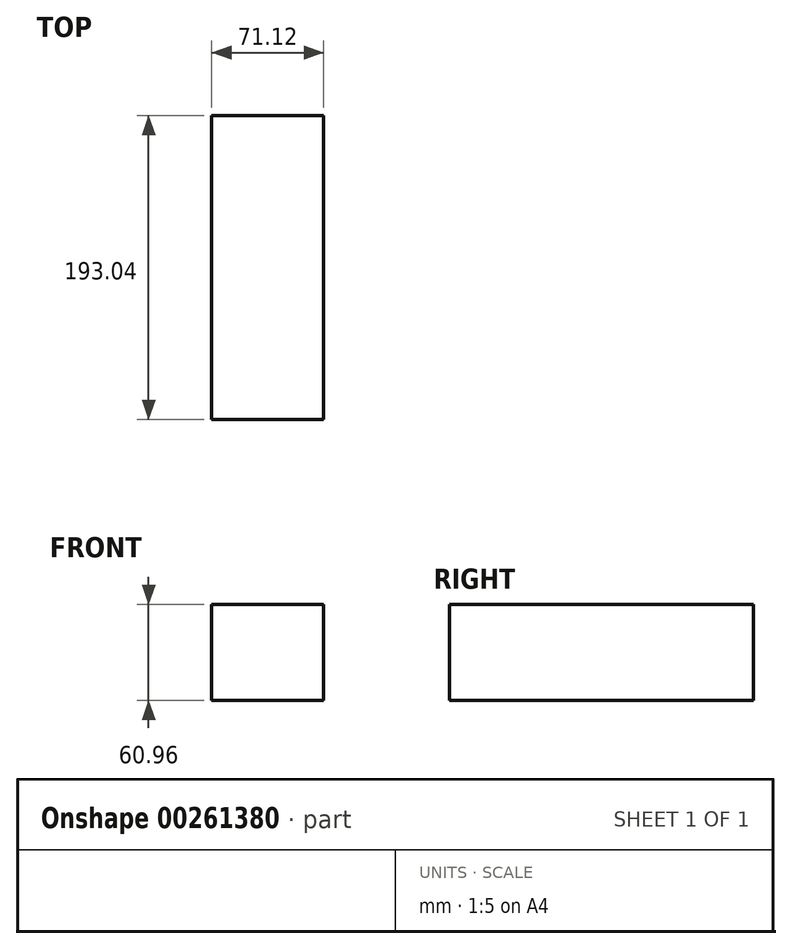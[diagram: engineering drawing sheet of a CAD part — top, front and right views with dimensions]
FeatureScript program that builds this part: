
annotation { "Feature Type Name" : "Feature", "Feature Type Description" : "" }
export const myFeature = defineFeature(function(context is Context, id is Id, definition is map)
    precondition{}
    {
        {
            var Q0;
            Q0=qCreatedBy(makeId("Top.planeOp"),FACE);
            var sketch = newSketch(context, id + "F0", { "sketchPlane" : qUnion([Q0])});
            skLineSegment(sketch, "E0.bottom", {"start": v(0, 0) * mm, "end": v(71.12, 0) * mm});
            skLineSegment(sketch, "E0.top", {"start": v(0, 193.04) * mm, "end": v(71.12, 193.04) * mm});
            skLineSegment(sketch, "E0.left", {"start": v(0, 0) * mm, "end": v(0, 193.04) * mm});
            skLineSegment(sketch, "E0.right", {"start": v(71.12, 0) * mm, "end": v(71.12, 193.04) * mm});
            skSolve(sketch);
        }
        {
            var Q0;
            Q0 = qSketchRegion(id + "F0", true);
            extrude(context, id + "F1", {"entities" : qUnion([Q0]), "depth" : 60.96 * mm});
        }
    });
